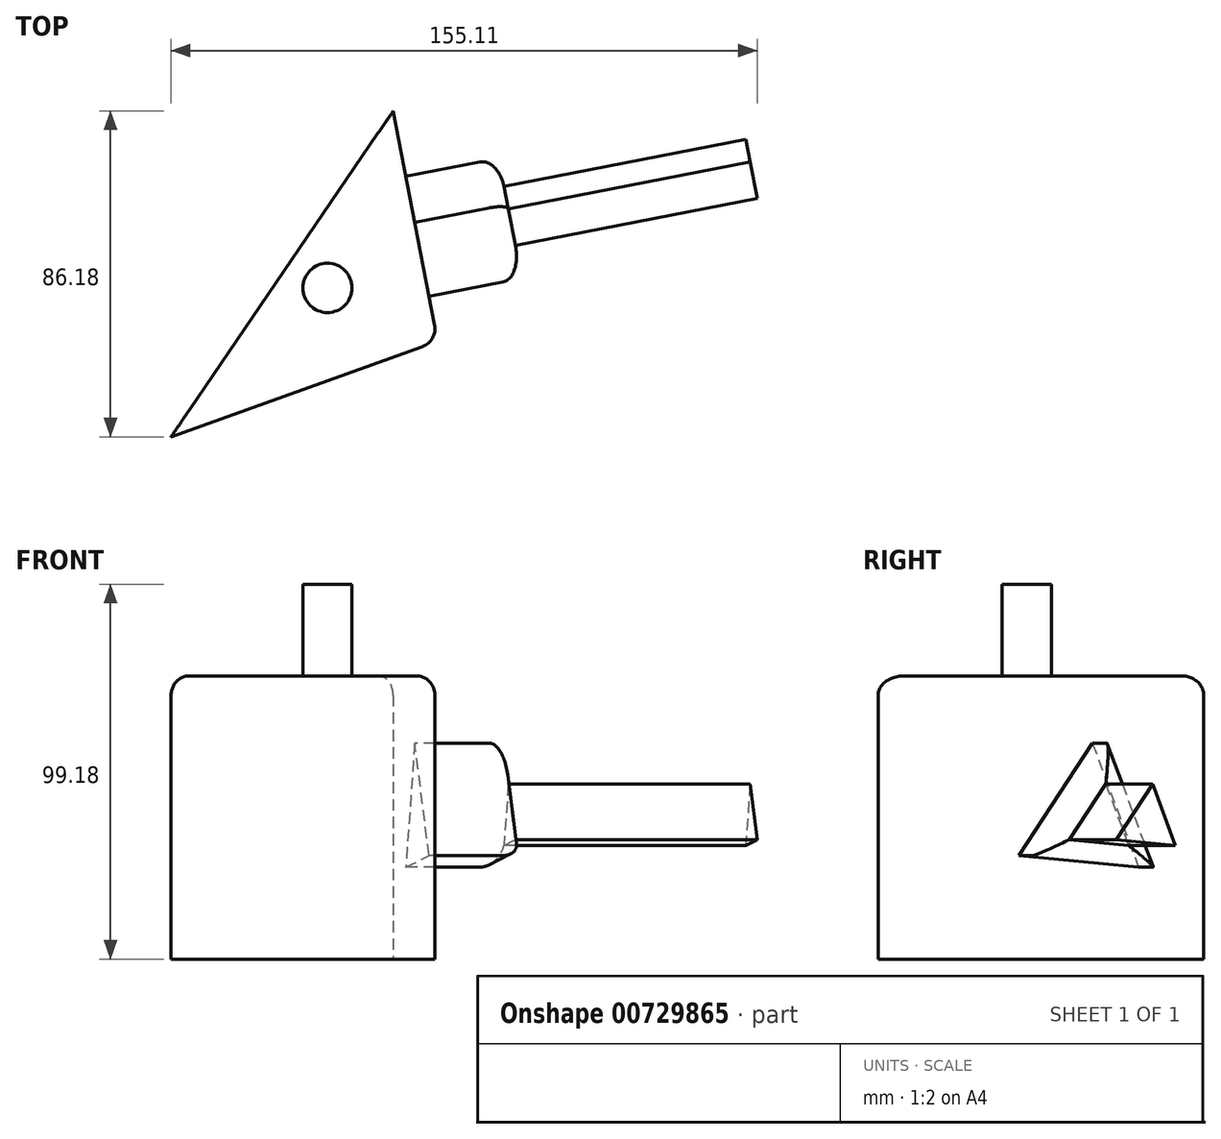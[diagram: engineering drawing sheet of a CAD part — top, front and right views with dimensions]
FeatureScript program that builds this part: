
annotation { "Feature Type Name" : "Feature", "Feature Type Description" : "" }
export const myFeature = defineFeature(function(context is Context, id is Id, definition is map)
    precondition{}
    {
        {
            var Q0;
            Q0=qCreatedBy(makeId("Top.planeOp"),FACE);
            var sketch = newSketch(context, id + "F0", { "sketchPlane" : qUnion([Q0])});
            skLineSegment(sketch, "E0", {"start": v(26.37, 35.65) * mm, "end": v(-32.41, -50.53) * mm});
            skLineSegment(sketch, "E1", {"start": v(-32.41, -50.53) * mm, "end": v(38.16, -25.2) * mm});
            skLineSegment(sketch, "E2", {"start": v(38.16, -25.2) * mm, "end": v(26.37, 35.65) * mm});
            skSolve(sketch);
        }
        {
            var Q0;
            Q0=makeQuery(id+"F0.imprint","IMPRINT",FACE,{"disambiguationData":[TD([[makeQuery(id+"F0.imprint","IMPRINT",EDGE,{"derivedFrom":sQuery(id+"F0.wireOp",EDGE,"E0")}),1.0]])]});
            extrude(context, id + "F1", {"entities" : qUnion([Q0]), "depth" : 74.94 * mm, "offsetDistance" : 25.4 * mm});
        }
        {
            var Q0;
            Q0=makeQuery(id+"F1.opExtrude","CAP_EDGE",EDGE,{"disambiguationData":[OSD([sQuery(id+"F0.wireOp",EDGE,"E1")])],"isStart":false});
            var Q1;
            Q1=makeQuery(id+"F1.opExtrude","CAP_EDGE",EDGE,{"disambiguationData":[OSD([sQuery(id+"F0.wireOp",EDGE,"E2")])],"isStart":false});
            var Q2;
            Q2=makeQuery(id+"F1.opExtrude","SWEPT_EDGE",EDGE,{"disambiguationData":[OSD([sQuery(id+"F0.wireOp",EDGE,"E1"),sQuery(id+"F0.wireOp",EDGE,"E2")])]});
            fillet(context, id + "F2", {"entities" : qUnion([Q0, Q1, Q2]), "radius" : 5.08 * mm, "tangentPropagation" : true, "allowEdgeOverflow" : false});
        }
        {
            var Q0;
            Q0=makeQuery(id+"F1.opExtrude","CAP_FACE",FACE,{"disambiguationData":[OSD([sQuery(id+"F0.wireOp",EDGE,"E0"),sQuery(id+"F0.wireOp",EDGE,"E1"),sQuery(id+"F0.wireOp",EDGE,"E2")])],"isStart":false});
            var sketch = newSketch(context, id + "F3", { "sketchPlane" : qUnion([Q0])});
            skCircle(sketch, "E3", {"center": v(8.98, -11.15) * mm, "radius": 6.52 * mm});
            skSolve(sketch);
        }
        {
            var Q0;
            Q0=makeQuery(id+"F3.imprint","IMPRINT",FACE,{"disambiguationData":[TD([[makeQuery(id+"F3.imprint","IMPRINT",EDGE,{"derivedFrom":sQuery(id+"F3.wireOp",EDGE,"E3")}),1.0]])]});
            extrude(context, id + "F4", {"entities" : qUnion([Q0]), "operationType" : NewBodyOperationType.ADD, "depth" : 24.24 * mm, "offsetDistance" : 25 * mm});
        }
        {
            var Q0;
            Q0=makeQuery(id+"F1.opExtrude","SWEPT_FACE",FACE,{"disambiguationData":[OSD([sQuery(id+"F0.wireOp",EDGE,"E2")])]});
            var sketch = newSketch(context, id + "F5", { "sketchPlane" : qUnion([Q0])});
            skLineSegment(sketch, "E4", {"start": v(-19.9, 27.4) * mm, "end": v(0, 57.15) * mm});
            skLineSegment(sketch, "E5", {"start": v(0, 57.15) * mm, "end": v(12.4, 24.31) * mm});
            skLineSegment(sketch, "E6", {"start": v(12.4, 24.31) * mm, "end": v(-19.9, 27.4) * mm});
            skSolve(sketch);
        }
        {
            var Q0;
            Q0=makeQuery(id+"F5.imprint","IMPRINT",FACE,{"disambiguationData":[TD([[makeQuery(id+"F5.imprint","IMPRINT",EDGE,{"derivedFrom":sQuery(id+"F5.wireOp",EDGE,"E4")}),-1.0]])]});
            extrude(context, id + "F6", {"entities" : qUnion([Q0]), "operationType" : NewBodyOperationType.ADD, "depth" : 25 * mm, "offsetDistance" : 25 * mm});
        }
        {
            var Q0;
            Q0=makeQuery(id+"F6.opExtrude","CAP_EDGE",EDGE,{"disambiguationData":[OSD([sQuery(id+"F5.wireOp",EDGE,"E5")])],"isStart":false});
            var Q1;
            Q1=makeQuery(id+"F6.opExtrude","CAP_EDGE",EDGE,{"disambiguationData":[OSD([sQuery(id+"F5.wireOp",EDGE,"E6")])],"isStart":false});
            var Q2;
            Q2=makeQuery(id+"F6.opExtrude","CAP_EDGE",EDGE,{"disambiguationData":[OSD([sQuery(id+"F5.wireOp",EDGE,"E4")])],"isStart":false});
            fillet(context, id + "F7", {"entities" : qUnion([Q0, Q1, Q2]), "radius" : 5 * mm, "tangentPropagation" : true, "allowEdgeOverflow" : false});
        }
        {
            var Q0;
            Q0=makeQuery(id+"F6.opExtrude","CAP_FACE",FACE,{"disambiguationData":[OSD([sQuery(id+"F5.wireOp",EDGE,"E4"),sQuery(id+"F5.wireOp",EDGE,"E5"),sQuery(id+"F5.wireOp",EDGE,"E6")])],"isStart":false});
            extrude(context, id + "F8", {"entities" : qUnion([Q0]), "operationType" : NewBodyOperationType.ADD, "depth" : 25 * mm, "offsetDistance" : 25 * mm});
        }
        {
            var Q0;
            Q0=makeQuery(id+"F8.opExtrude","CAP_FACE",FACE,{"disambiguationData":[OSD([sQuery(id+"F5.wireOp",EDGE,"E4"),sQuery(id+"F5.wireOp",EDGE,"E5"),sQuery(id+"F5.wireOp",EDGE,"E6")])],"isStart":false});
            extrude(context, id + "F9", {"entities" : qUnion([Q0]), "operationType" : NewBodyOperationType.ADD, "depth" : 40.16 * mm, "offsetDistance" : 25 * mm});
        }
    });
